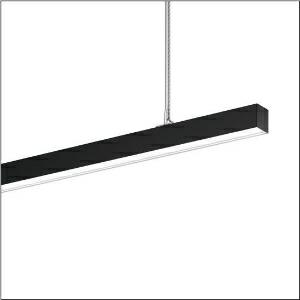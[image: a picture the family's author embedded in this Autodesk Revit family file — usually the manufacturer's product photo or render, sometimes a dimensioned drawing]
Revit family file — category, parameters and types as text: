
# Revit family: silica_r__21_51mx33db49bb_8fe2
name_source: partatom
category: Lighting Fixtures
units: mm (PartAtom-declared; Revit-internal decimal feet)

## family parameters
Cut with Voids When Loaded = No
Host = Face
Light Source = No
Part Type = Normal
Room Calculation Point = No
Round Connector Dimension = Use Diameter
Shared = No

## types (1)
- --- (1 x LED, 7390 lm, 48.3 W, 4000K)
    Apparent Load = 48 VA
    CIE Flux Codes = 78 96 99 55 100
    Color Rendering = 80
    Color Temperature = 4000K
    Default Elevation = 1800 mm
    Description = Silica® 21, office luminaire, primary optical cover: prismatic diffuser, of PMMA, CAT 2 (L<= 3000cd/m²), light emission: direct/indirect distribution, primary light characteristic: symmetric, installation type: suspended mounting, LED, rated luminous flux: 7.390lm, luminous efficacy: 153lm/W, light colour: 840, colour temperature: 4000K, control gear: DALI 2, with terminal, 3+2-pole, max. 2.5mm², mains connection: 220..240V, AC, 50/60Hz, rated input power: 48.3W, luminaire housing, of aluminium, matt jet black (RAL 9005), length: 1.504mm, width: 53mm, height: 53mm, protection rating (complete): IP20, insulation class (complete): insulation class I (protective earthing), certification: CE, permissible operating ambient temperature: 0..+35°C, standard: EN 50419, packaging unit: 1 piece
    Height = 53 mm
    Lamp = 1 x LED
    Lamp Light Flux = 7390 lm
    Lamp Power = 48.3 W
    Lamp count = 1
    Length = 1504 mm
    Luminous efficacy = 153 lm/W
    Manufacturer = Siteco
    ModVariant = No
    Model = 51MX33DB49BB
    Mounting Place = Ceiling
    Mounting Type = Pendant
    Number of Poles = 1
    OnlyDefault = Yes
    Power Factor = 1
    Product Name = Silica® 21
    Product group = office luminaire | ceiling pendant
    ProductGroupID = 904
    Protection Class = Protection class I
    Protection Degree = IP 20
    RLX_Detail_Level = 1
    RLX_Emergency_Light_Flux = 0 lm
    RLX_Emergency_Type = 0
    RLX_Emergency_Type_DB = No
    RlxData = <blob elided: 26341 chars, md5=0df9e98c>
    Socket = socket
    Standby Power = 0 W
    System Light Flux = 7390 lm
    System Power = 48 W
    Type Comments = factory setting: luminous flux: 100 % | dim-lin: 254 | 323 mA
    Type Image = l_1335856.jpg
    URL = http://relux.com
    VarID = @adj_118420
    Voltage = 0 V
    Weight = 0.00 kg
    Width = 53 mm

## geometry (parser evidence)
native form markers: Blend x4, Sweep x14
no freeform markers — native parametric forms only
